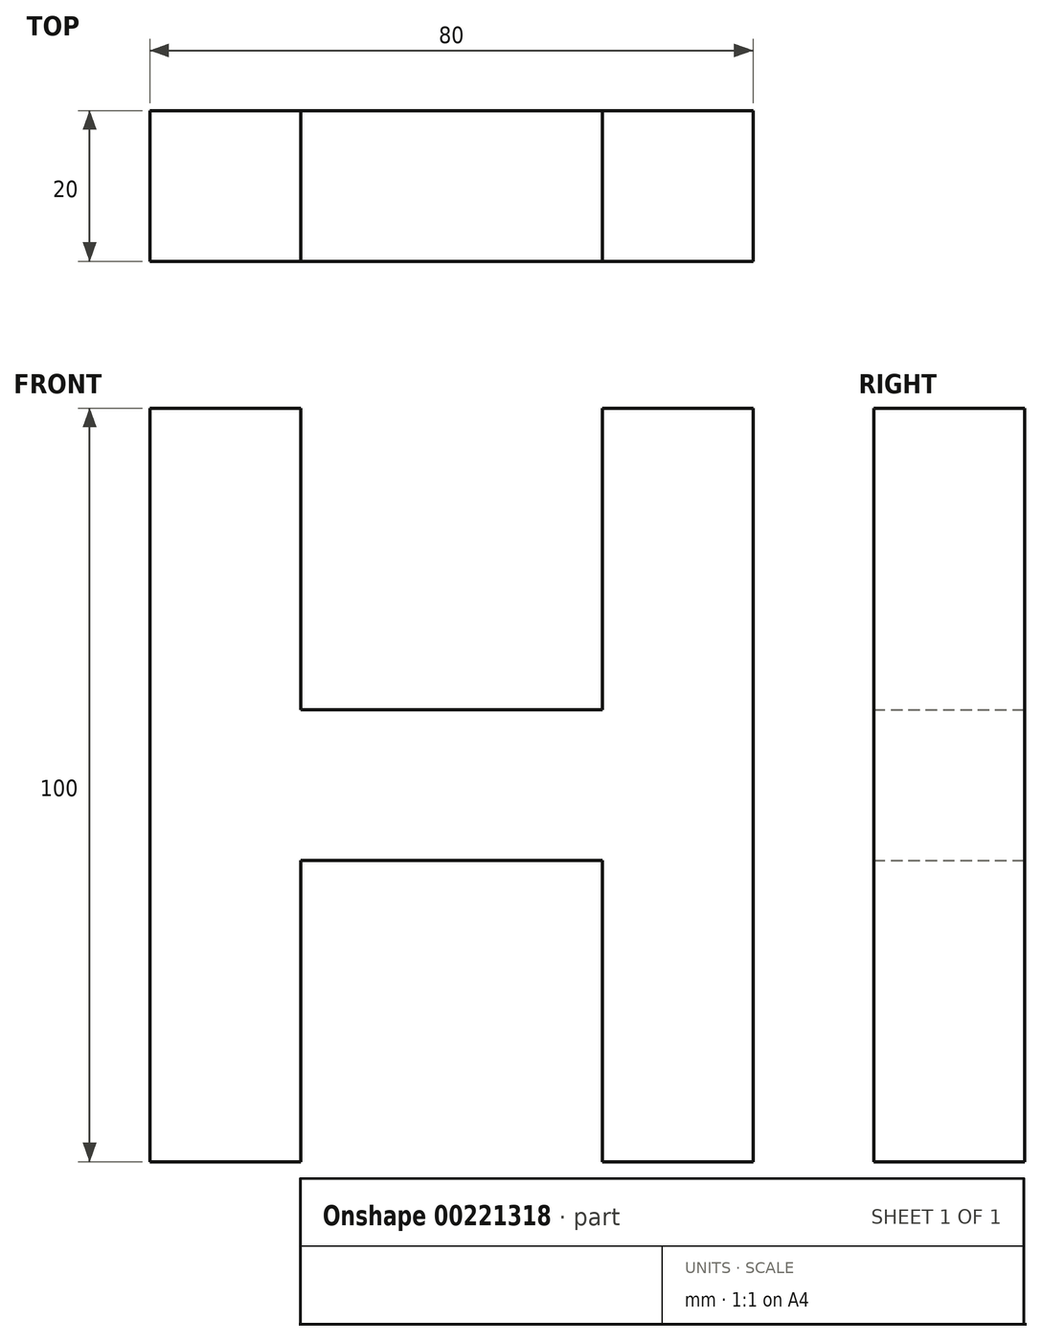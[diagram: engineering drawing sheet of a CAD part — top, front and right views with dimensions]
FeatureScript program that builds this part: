
annotation { "Feature Type Name" : "Feature", "Feature Type Description" : "" }
export const myFeature = defineFeature(function(context is Context, id is Id, definition is map)
    precondition{}
    {
        {
            var Q0;
            Q0=qCreatedBy(makeId("Front.planeOp"),FACE);
            var sketch = newSketch(context, id + "F0", { "sketchPlane" : qUnion([Q0])});
            skLineSegment(sketch, "E0", {"start": v(0, 100) * mm, "end": v(0, 0) * mm});
            skLineSegment(sketch, "E1", {"start": v(0, 0) * mm, "end": v(20, 0) * mm});
            skLineSegment(sketch, "E2", {"start": v(20, 0) * mm, "end": v(20, 40) * mm});
            skLineSegment(sketch, "E3", {"start": v(20, 40) * mm, "end": v(60, 40) * mm});
            skLineSegment(sketch, "E4", {"start": v(60, 40) * mm, "end": v(60, 0) * mm});
            skLineSegment(sketch, "E5", {"start": v(60, 0) * mm, "end": v(80, 0) * mm});
            skLineSegment(sketch, "E6", {"start": v(80, 0) * mm, "end": v(80, 100) * mm});
            skLineSegment(sketch, "E7", {"start": v(80, 100) * mm, "end": v(60, 100) * mm});
            skLineSegment(sketch, "E8", {"start": v(60, 100) * mm, "end": v(60, 60) * mm});
            skLineSegment(sketch, "E9", {"start": v(60, 60) * mm, "end": v(20, 60) * mm});
            skLineSegment(sketch, "E10", {"start": v(20, 60) * mm, "end": v(20, 100) * mm});
            skLineSegment(sketch, "E11", {"start": v(20, 100) * mm, "end": v(0, 100) * mm});
            skSolve(sketch);
        }
        {
            var Q0;
            Q0 = qSketchRegion(id + "F0", true);
            extrude(context, id + "F1", {"entities" : qUnion([Q0]), "depth" : 20 * mm});
        }
    });
